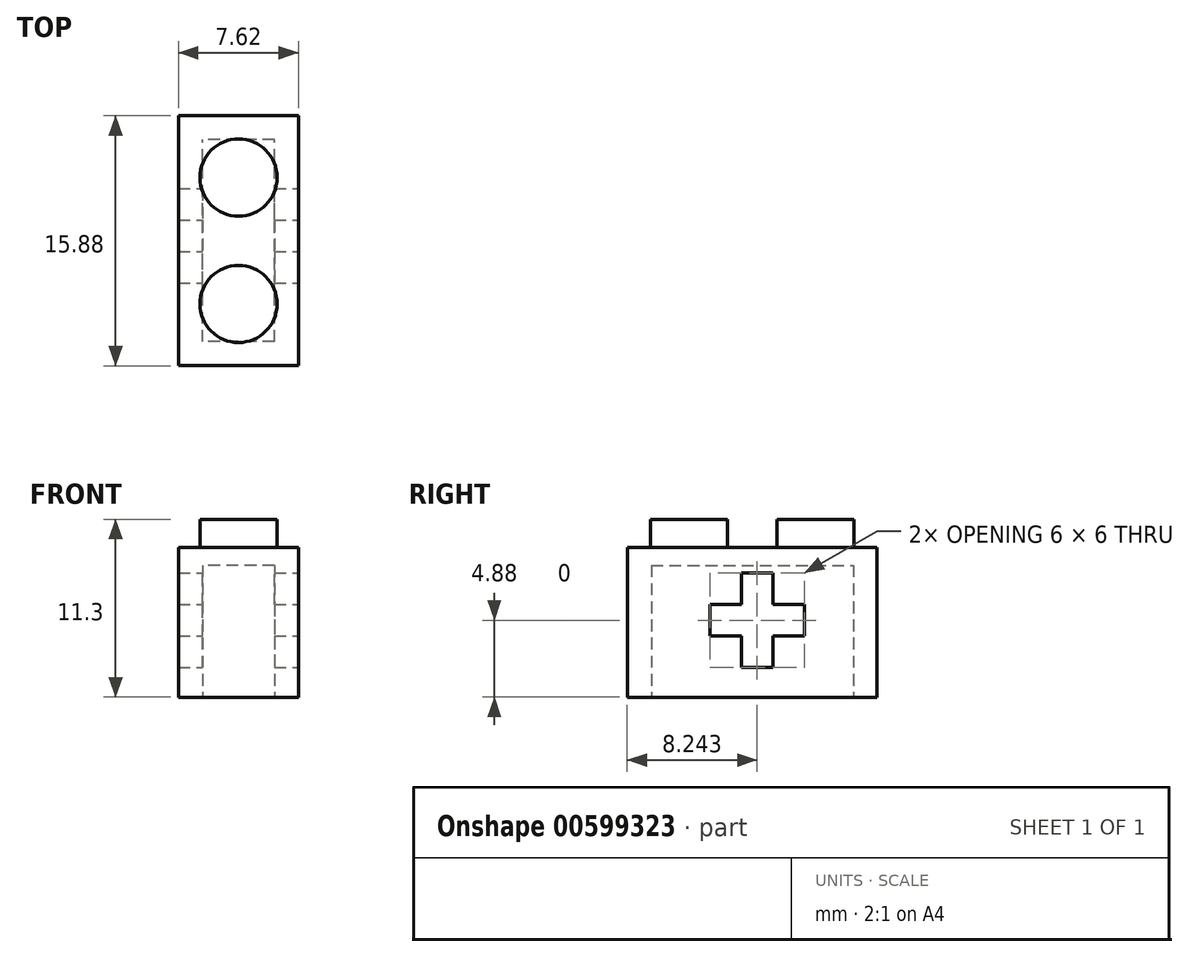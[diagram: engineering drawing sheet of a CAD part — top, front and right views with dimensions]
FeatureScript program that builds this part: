
annotation { "Feature Type Name" : "Feature", "Feature Type Description" : "" }
export const myFeature = defineFeature(function(context is Context, id is Id, definition is map)
    precondition{}
    {
        {
            var Q0;
            Q0=qCreatedBy(makeId("Top.planeOp"),FACE);
            var sketch = newSketch(context, id + "F0", { "sketchPlane" : qUnion([Q0])});
            skLineSegment(sketch, "E0.bottom", {"start": v(3.81, 7.94) * mm, "end": v(-3.8, 7.94) * mm});
            skLineSegment(sketch, "E0.top", {"start": v(3.8, -7.94) * mm, "end": v(-3.81, -7.94) * mm});
            skLineSegment(sketch, "E0.left", {"start": v(3.81, 7.94) * mm, "end": v(3.8, -7.94) * mm});
            skLineSegment(sketch, "E0.right", {"start": v(-3.8, 7.94) * mm, "end": v(-3.81, -7.94) * mm});
            skPoint(sketch, "E0.middle", {"position": v(0, 0) * mm});
            skSolve(sketch);
        }
        {
            var Q0;
            Q0=makeQuery(id+"F0.imprint","IMPRINT",FACE,{"disambiguationData":[TD([[makeQuery(id+"F0.imprint","IMPRINT",EDGE,{"derivedFrom":sQuery(id+"F0.wireOp",EDGE,"E0.bottom")}),1.0]])]});
            extrude(context, id + "F1", {"entities" : qUnion([Q0]), "endBound" : BoundingType.SYMMETRIC, "depth" : 9.52 * mm, "offsetDistance" : 25 * mm});
        }
        {
            var Q0;
            Q0=makeQuery(id+"F1.opExtrude","CAP_FACE",FACE,{"disambiguationData":[OSD([sQuery(id+"F0.wireOp",EDGE,"E0.bottom"),sQuery(id+"F0.wireOp",EDGE,"E0.top"),sQuery(id+"F0.wireOp",EDGE,"E0.left"),sQuery(id+"F0.wireOp",EDGE,"E0.right")])],"isStart":false});
            var sketch = newSketch(context, id + "F2", { "sketchPlane" : qUnion([Q0])});
            skCircle(sketch, "E1", {"center": v(0, 4.01) * mm, "radius": 2.45 * mm});
            skCircle(sketch, "E2", {"center": v(0, -4.01) * mm, "radius": 2.45 * mm});
            skSolve(sketch);
        }
        {
            var Q0;
            Q0=makeQuery(id+"F2.imprint","IMPRINT",FACE,{"disambiguationData":[TD([[makeQuery(id+"F2.imprint","IMPRINT",EDGE,{"derivedFrom":sQuery(id+"F2.wireOp",EDGE,"E1")}),1.0]])]});
            var Q1;
            Q1=makeQuery(id+"F2.imprint","IMPRINT",FACE,{"disambiguationData":[TD([[makeQuery(id+"F2.imprint","IMPRINT",EDGE,{"derivedFrom":sQuery(id+"F2.wireOp",EDGE,"E2")}),1.0]])]});
            extrude(context, id + "F3", {"entities" : qUnion([Q0, Q1]), "operationType" : NewBodyOperationType.ADD, "depth" : 1.78 * mm});
        }
        {
            var Q0;
            Q0=makeQuery(id+"F1.opExtrude","CAP_FACE",FACE,{"disambiguationData":[OSD([sQuery(id+"F0.wireOp",EDGE,"E0.bottom"),sQuery(id+"F0.wireOp",EDGE,"E0.top"),sQuery(id+"F0.wireOp",EDGE,"E0.left"),sQuery(id+"F0.wireOp",EDGE,"E0.right")])],"isStart":true});
            var sketch = newSketch(context, id + "F4", { "sketchPlane" : qUnion([Q0])});
            skLineSegment(sketch, "E3.bottom", {"start": v(2.29, 6.41) * mm, "end": v(-2.29, 6.41) * mm});
            skLineSegment(sketch, "E3.top", {"start": v(2.29, -6.41) * mm, "end": v(-2.29, -6.41) * mm});
            skLineSegment(sketch, "E3.left", {"start": v(2.29, 6.41) * mm, "end": v(2.29, -6.41) * mm});
            skLineSegment(sketch, "E3.right", {"start": v(-2.29, 6.41) * mm, "end": v(-2.29, -6.41) * mm});
            skSolve(sketch);
        }
        {
            var Q0;
            Q0=makeQuery(id+"F4.imprint","IMPRINT",FACE,{"disambiguationData":[TD([[makeQuery(id+"F4.imprint","IMPRINT",EDGE,{"derivedFrom":sQuery(id+"F4.wireOp",EDGE,"E3.bottom")}),1.0]])]});
            extrude(context, id + "F5", {"entities" : qUnion([Q0]), "operationType" : NewBodyOperationType.REMOVE, "oppositeDirection" : true, "depth" : 8.38 * mm});
        }
        {
            var Q0;
            Q0=makeQuery(id+"F1.opExtrude","SWEPT_FACE",FACE,{"disambiguationData":[OSD([sQuery(id+"F0.wireOp",EDGE,"E0.left")])]});
            var sketch = newSketch(context, id + "F6", { "sketchPlane" : qUnion([Q0])});
            skLineSegment(sketch, "E4", {"start": v(-0.7, 3.12) * mm, "end": v(1.3, 3.12) * mm});
            skLineSegment(sketch, "E5", {"start": v(1.3, 3.12) * mm, "end": v(1.3, 1.12) * mm});
            skLineSegment(sketch, "E6", {"start": v(1.3, 1.12) * mm, "end": v(3.3, 1.12) * mm});
            skLineSegment(sketch, "E7", {"start": v(3.3, 1.12) * mm, "end": v(3.3, -0.88) * mm});
            skLineSegment(sketch, "E8", {"start": v(3.3, -0.88) * mm, "end": v(1.3, -0.88) * mm});
            skLineSegment(sketch, "E9", {"start": v(1.3, -0.88) * mm, "end": v(1.3, -2.88) * mm});
            skLineSegment(sketch, "E10", {"start": v(1.3, -2.88) * mm, "end": v(-0.7, -2.88) * mm});
            skLineSegment(sketch, "E11", {"start": v(-0.7, -2.88) * mm, "end": v(-0.7, -0.88) * mm});
            skLineSegment(sketch, "E12", {"start": v(-0.7, -0.88) * mm, "end": v(-2.7, -0.88) * mm});
            skLineSegment(sketch, "E13", {"start": v(-2.7, -0.88) * mm, "end": v(-2.7, 1.12) * mm});
            skLineSegment(sketch, "E14", {"start": v(-2.7, 1.12) * mm, "end": v(-0.7, 1.12) * mm});
            skLineSegment(sketch, "E15", {"start": v(-0.7, 1.12) * mm, "end": v(-0.7, 3.12) * mm});
            skSolve(sketch);
        }
        {
            var Q0;
            Q0=makeQuery(id+"F6.imprint","IMPRINT",FACE,{"disambiguationData":[TD([[makeQuery(id+"F6.imprint","IMPRINT",EDGE,{"derivedFrom":sQuery(id+"F6.wireOp",EDGE,"E4")}),-1.0]])]});
            extrude(context, id + "F7", {"entities" : qUnion([Q0]), "operationType" : NewBodyOperationType.REMOVE, "oppositeDirection" : true, "depth" : 7.77 * mm, "offsetDistance" : 25 * mm});
        }
    });
